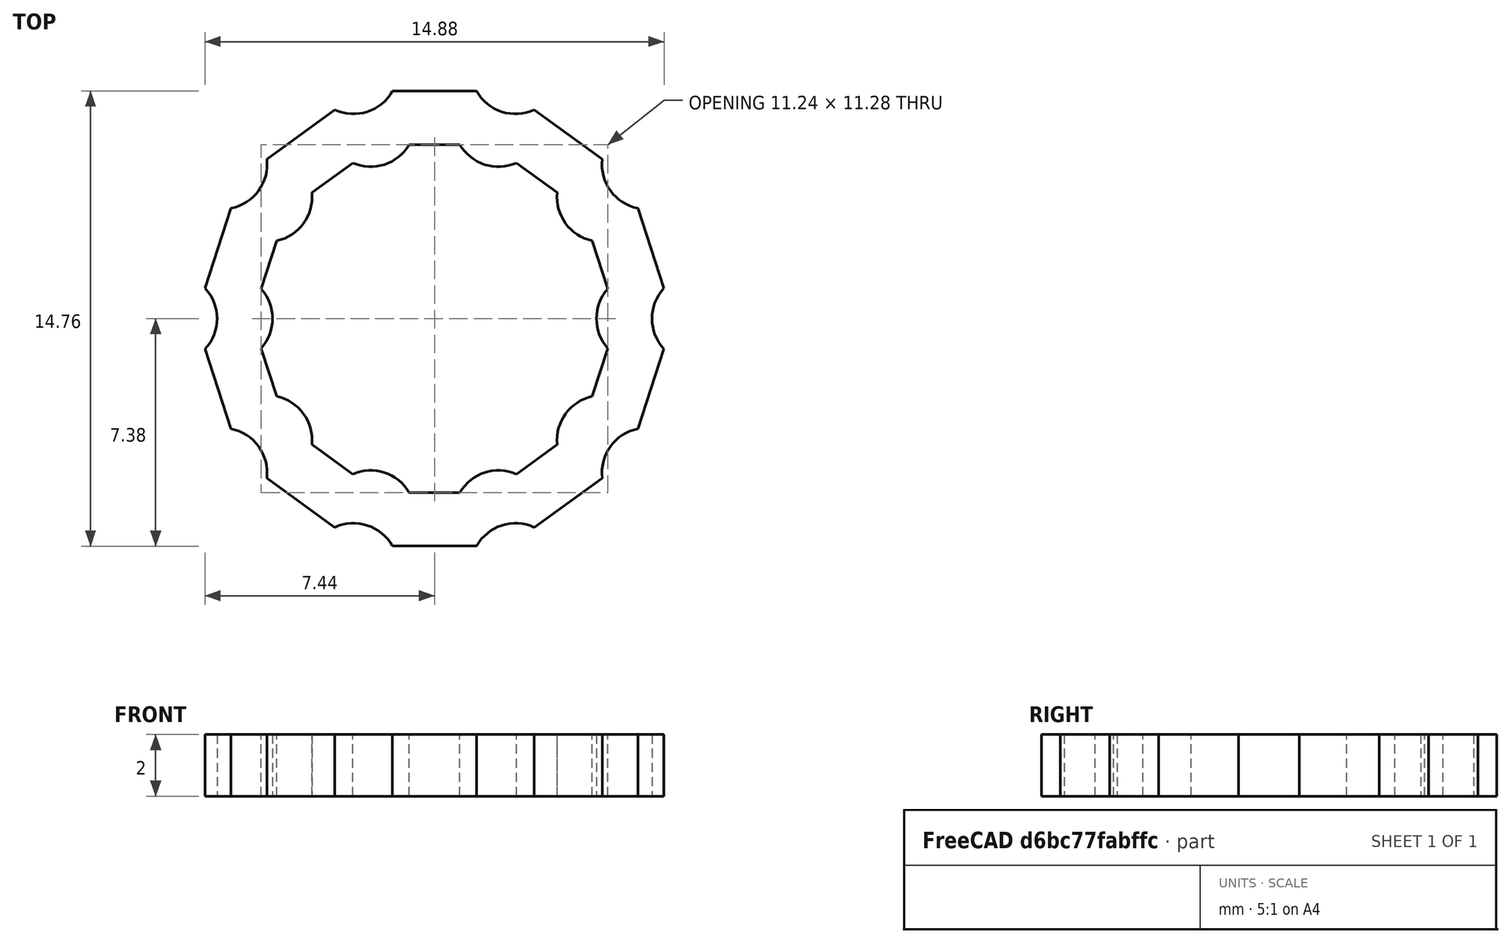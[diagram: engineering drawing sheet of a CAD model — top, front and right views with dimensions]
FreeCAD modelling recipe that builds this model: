
FCSTD DOCUMENT  (FreeCAD 0.19R)
Label: luer_lock_marker
License: All rights reserved
LicenseURL: http://en.wikipedia.org/wiki/All_rights_reserved
objects: Spreadsheet::Sheet×1, Sketcher::SketchObject×1, PartDesign::Pad×1, PartDesign::Body×1
note: 4 computed .brp shape members not serialized (recipe doc carries the construction recipe); baked Part::Feature solids carry a one-line shape summary decoded from their .brp

FEATURE [Spreadsheet::Sheet] Spreadsheet  label="var"
  cells = A1=thickness; B1(thickness)=1.8; A2=inner_radius; B2(inner_radius)=5.7000000000000002; A3=outer_radius; B3(outer_radius)==inner_radius + 1
FEATURE [Sketcher::SketchObject] CopySketch002  label="marker sketch"
  expr: Constraints[60] = <<var>>.outer_radius + <<var>>.thickness
  expr: Constraints[59] = <<var>>.inner_radius + <<var>>.thickness
  expr: Constraints[122] = <<var>>.outer_radius
  expr: Constraints[121] = <<var>>.inner_radius
  sketch-geometry (44):
    g0: Circle [constr] CenterX=0 CenterY=0 CenterZ=0 NormalX=0 NormalY=0 NormalZ=1 AngleXU=0 Radius=7.5
    g1: ArcOfCircle CenterX=2.62664 CenterY=8.08398 CenterZ=0 NormalX=0 NormalY=0 NormalZ=1 AngleXU=0 Radius=1.45 StartAngle=3.65219 EndAngle=5.14427
    g2: ArcOfCircle CenterX=6.87664 CenterY=4.99617 CenterZ=0 NormalX=0 NormalY=0 NormalZ=1 AngleXU=0 Radius=1.45 StartAngle=3.02387 EndAngle=4.51595
    g3: ArcOfCircle CenterX=6.87664 CenterY=-4.99617 CenterZ=0 NormalX=0 NormalY=0 NormalZ=1 AngleXU=0 Radius=1.45 StartAngle=1.76723 EndAngle=3.25932
    g4: ArcOfCircle CenterX=2.62664 CenterY=-8.08398 CenterZ=0 NormalX=0 NormalY=0 NormalZ=1 AngleXU=0 Radius=1.45 StartAngle=1.13891 EndAngle=2.631
    g5: ArcOfCircle CenterX=-2.62664 CenterY=-8.08398 CenterZ=0 NormalX=0 NormalY=0 NormalZ=1 AngleXU=0 Radius=1.45 StartAngle=0.510595 EndAngle=2.00268
    g6: ArcOfCircle CenterX=-6.87664 CenterY=-4.99617 CenterZ=0 NormalX=0 NormalY=0 NormalZ=1 AngleXU=0 Radius=1.45 StartAngle=6.16546 EndAngle=7.65755
    g7: ArcOfCircle CenterX=-8.5 CenterY=7e-16 CenterZ=0 NormalX=0 NormalY=0 NormalZ=1 AngleXU=0 Radius=1.45 StartAngle=5.53714 EndAngle=7.02923
    g8: ArcOfCircle CenterX=-6.87664 CenterY=4.99617 CenterZ=0 NormalX=0 NormalY=0 NormalZ=1 AngleXU=0 Radius=1.45 StartAngle=4.90883 EndAngle=6.40091
    g9: ArcOfCircle CenterX=-2.62664 CenterY=8.08398 CenterZ=0 NormalX=0 NormalY=0 NormalZ=1 AngleXU=0 Radius=1.45 StartAngle=4.28051 EndAngle=5.77259
    g10: ArcOfCircle CenterX=8.5 CenterY=0 CenterZ=0 NormalX=0 NormalY=0 NormalZ=1 AngleXU=0 Radius=1.45 StartAngle=2.39555 EndAngle=3.88763
    g11: Circle [constr] CenterX=0 CenterY=0 CenterZ=0 NormalX=0 NormalY=0 NormalZ=1 AngleXU=0 Radius=8.5
    g12: LineSegment StartX=-5.43668 StartY=5.16648 StartZ=0 EndX=-3.23359 EndY=6.76712 EndZ=0
    g13: LineSegment StartX=-1.36159 StartY=7.37537 StartZ=0 EndX=1.36159 EndY=7.37537 EndZ=0
    g14: LineSegment StartX=3.23359 StartY=6.76712 StartZ=0 EndX=5.43668 EndY=5.16648 EndZ=0
    g15: LineSegment StartX=6.59364 StartY=3.57406 StartZ=0 EndX=7.43515 EndY=0.984169 EndZ=0
    g16: LineSegment StartX=7.43515 StartY=-0.984169 StartZ=0 EndX=6.59364 EndY=-3.57406 EndZ=0
    g17: LineSegment StartX=3.23359 StartY=-6.76712 StartZ=0 EndX=5.43668 EndY=-5.16648 EndZ=0
    g18: LineSegment StartX=-1.36159 StartY=-7.37537 StartZ=0 EndX=1.36159 EndY=-7.37537 EndZ=0
    g19: LineSegment StartX=-5.43668 StartY=-5.16648 StartZ=0 EndX=-3.23359 EndY=-6.76712 EndZ=0
    g20: LineSegment StartX=-7.43515 StartY=-0.984169 StartZ=0 EndX=-6.59364 EndY=-3.57406 EndZ=0
    g21: LineSegment StartX=-6.59364 StartY=3.57406 StartZ=0 EndX=-7.43515 EndY=0.984169 EndZ=0
    g22: Circle [constr] CenterX=0 CenterY=0 CenterZ=0 NormalX=0 NormalY=0 NormalZ=1 AngleXU=0 Radius=6.7
    g23: Circle [constr] CenterX=0 CenterY=0 CenterZ=0 NormalX=0 NormalY=0 NormalZ=1 AngleXU=0 Radius=5.7
    g24: LineSegment StartX=5.61772 StartY=-0.964976 StartZ=0 EndX=5.11203 EndY=-2.52133 EndZ=0
    g25: LineSegment StartX=3.97764 StartY=-4.0827 StartZ=0 EndX=2.65372 EndY=-5.04458 EndZ=0
    g26: LineSegment StartX=0.818226 StartY=-5.64097 StartZ=0 EndX=-0.818226 EndY=-5.64097 EndZ=0
    g27: LineSegment StartX=-2.65372 StartY=-5.04458 StartZ=0 EndX=-3.97764 EndY=-4.0827 EndZ=0
    g28: LineSegment StartX=-5.11203 StartY=-2.52133 StartZ=0 EndX=-5.61772 EndY=-0.964976 EndZ=0
    g29: LineSegment StartX=-5.61772 StartY=0.964976 StartZ=0 EndX=-5.11203 EndY=2.52133 EndZ=0
    g30: LineSegment StartX=-3.97764 StartY=4.0827 StartZ=0 EndX=-2.65372 EndY=5.04458 EndZ=0
    g31: LineSegment StartX=-0.818226 StartY=5.64097 StartZ=0 EndX=0.818226 EndY=5.64097 EndZ=0
    g32: LineSegment StartX=2.65372 StartY=5.04458 StartZ=0 EndX=3.97764 EndY=4.0827 EndZ=0
    g33: LineSegment StartX=5.11203 StartY=2.52133 StartZ=0 EndX=5.61772 EndY=0.964976 EndZ=0
    g34: ArcOfCircle CenterX=5.42041 CenterY=-3.93816 CenterZ=0 NormalX=0 NormalY=0 NormalZ=1 AngleXU=0 Radius=1.45 StartAngle=1.78511 EndAngle=3.24144
    g35: ArcOfCircle CenterX=2.07041 CenterY=-6.37208 CenterZ=0 NormalX=0 NormalY=0 NormalZ=1 AngleXU=0 Radius=1.45 StartAngle=1.15679 EndAngle=2.61312
    g36: ArcOfCircle CenterX=-2.07041 CenterY=-6.37208 CenterZ=0 NormalX=0 NormalY=0 NormalZ=1 AngleXU=0 Radius=1.45 StartAngle=0.528473 EndAngle=1.9848
    g37: ArcOfCircle CenterX=-5.42041 CenterY=-3.93816 CenterZ=0 NormalX=0 NormalY=0 NormalZ=1 AngleXU=0 Radius=1.45 StartAngle=6.18334 EndAngle=7.63967
    g38: ArcOfCircle CenterX=-6.7 CenterY=-2.1e-15 CenterZ=0 NormalX=0 NormalY=0 NormalZ=1 AngleXU=0 Radius=1.45 StartAngle=5.55502 EndAngle=7.01135
    g39: ArcOfCircle CenterX=-5.42041 CenterY=3.93816 CenterZ=0 NormalX=0 NormalY=0 NormalZ=1 AngleXU=0 Radius=1.45 StartAngle=4.9267 EndAngle=6.38303
    g40: ArcOfCircle CenterX=-2.07041 CenterY=6.37208 CenterZ=0 NormalX=0 NormalY=0 NormalZ=1 AngleXU=0 Radius=1.45 StartAngle=4.29838 EndAngle=5.75471
    g41: ArcOfCircle CenterX=2.07041 CenterY=6.37208 CenterZ=0 NormalX=0 NormalY=0 NormalZ=1 AngleXU=0 Radius=1.45 StartAngle=3.67007 EndAngle=5.12639
    g42: ArcOfCircle CenterX=5.42041 CenterY=3.93816 CenterZ=0 NormalX=0 NormalY=0 NormalZ=1 AngleXU=0 Radius=1.45 StartAngle=3.04175 EndAngle=4.49808
    g43: ArcOfCircle CenterX=6.7 CenterY=0 CenterZ=0 NormalX=0 NormalY=0 NormalZ=1 AngleXU=0 Radius=1.45 StartAngle=2.41343 EndAngle=3.86976
  constraints (142):
    c: PointOnObject(g1,g0)
    c: PointOnObject(g1,g0)
    c: PointOnObject(g2,g0)
    c: PointOnObject(g2,g0)
    c: PointOnObject(g3,g0)
    c: PointOnObject(g3,g0)
    c: PointOnObject(g4,g0)
    c: PointOnObject(g4,g0)
    c: PointOnObject(g5,g0)
    c: PointOnObject(g5,g0)
    c: PointOnObject(g6,g0)
    c: PointOnObject(g6,g0)
    c: PointOnObject(g7,g0)
    c: PointOnObject(g7,g0)
    c: PointOnObject(g8,g0)
    c: PointOnObject(g9,g0)
    c: PointOnObject(g9,g0)
    c: PointOnObject(g10,g0)
    c: PointOnObject(g10,g0)
    c: Equal(g1,g2)
    c: Equal(g1,g10)
    c: Equal(g1, g3-g9) x7
    c: PointOnObject(g1,g11)
    c: PointOnObject(g2,g11)
    c: PointOnObject(g10,g11)
    c: PointOnObject(g3,g11)
    c: PointOnObject(g4,g11)
    c: PointOnObject(g5,g11)
    c: PointOnObject(g6,g11)
    c: PointOnObject(g7,g11)
    c: PointOnObject(g8,g11)
    c: PointOnObject(g9,g11)
    c: Coincident(g12,g8)
    c: Coincident(g12,g9)
    c: Coincident(g13,g9)
    c: Coincident(g13,g1)
    c: Coincident(g14,g1)
    c: Coincident(g14,g2)
    c: PointOnObject(g8,g0)
    c: Coincident(g15,g2)
    c: Coincident(g16,g10)
    c: Coincident(g17,g4)
    c: Coincident(g17,g3)
    c: Coincident(g18,g5)
    c: Coincident(g18,g4)
    c: Coincident(g19,g6)
    c: Coincident(g19,g5)
    c: Coincident(g20,g7)
    c: Coincident(g20,g6)
    c: Coincident(g21,g8)
    c: Coincident(g15,g10)
    c: Coincident(g16,g3)
    c: Coincident(g21,g7)
    c: Radius(g0) = 7.5
    c: Radius(g11) = 8.5
    c: Equal(g16,g15)
    c: Equal(g15,g14)
    c: Equal(g14,g13)
    c: Equal(g13,g12)
    c: Equal(g12,g21)
    c: Equal(g21,g20)
    c: Equal(g20,g19)
    c: Equal(g19,g18)
    c: Equal(g18,g17)
    c: Radius(g2) = 1.45
    c: Coincident(g0,g11)
    c: PointOnObject(g24,g23)
    c: PointOnObject(g24,g23)
    c: PointOnObject(g25,g23)
    c: PointOnObject(g25,g23)
    c: PointOnObject(g26,g23)
    c: PointOnObject(g26,g23)
    c: PointOnObject(g27,g23)
    c: PointOnObject(g27,g23)
    c: PointOnObject(g28,g23)
    c: PointOnObject(g28,g23)
    c: PointOnObject(g29,g23)
    c: PointOnObject(g29,g23)
    c: PointOnObject(g30,g23)
    c: PointOnObject(g30,g23)
    c: PointOnObject(g31,g23)
    c: PointOnObject(g31,g23)
    c: PointOnObject(g32,g23)
    c: PointOnObject(g32,g23)
    c: PointOnObject(g33,g23)
    c: PointOnObject(g33,g23)
    c: PointOnObject(g34,g22)
    c: Coincident(g34,g25)
    c: Coincident(g34,g24)
    c: PointOnObject(g35,g22)
    c: Coincident(g35,g25)
    c: Coincident(g35,g26)
    c: PointOnObject(g36,g22)
    c: Coincident(g36,g26)
    c: Coincident(g36,g27)
    c: PointOnObject(g37,g22)
    c: Coincident(g37,g27)
    c: Coincident(g37,g28)
    c: PointOnObject(g38,g22)
    c: Coincident(g38,g28)
    c: Coincident(g38,g29)
    c: PointOnObject(g39,g22)
    c: Coincident(g39,g29)
    c: Coincident(g39,g30)
    c: PointOnObject(g40,g22)
    c: Coincident(g40,g30)
    c: Coincident(g40,g31)
    c: Coincident(g41,g31)
    c: Coincident(g41,g32)
    c: PointOnObject(g42,g22)
    c: Coincident(g42,g32)
    c: Coincident(g42,g33)
    c: PointOnObject(g43,g22)
    c: Coincident(g43,g33)
    c: Coincident(g43,g24)
    c: Radius(g23) = 5.7
    c: Radius(g22) = 6.7
    c: PointOnObject(g41,g22)
    c: Equal(g24,g25)
    c: Equal(g25,g26)
    c: Equal(g26,g27)
    c: Equal(g27,g28)
    c: Equal(g28,g29)
    c: Equal(g29,g30)
    c: Equal(g30,g31)
    c: Equal(g31,g32)
    c: Equal(g32,g33)
    c: Equal(g34,g43)
    c: Equal(g43,g42)
    c: Equal(g42,g41)
    c: Equal(g41,g40)
    c: Equal(g40,g39)
    c: Equal(g39,g38)
    c: Equal(g38,g37)
    c: Equal(g37,g36)
    c: Equal(g36,g35)
    c: Radius(g43) = 1.45
    c: Coincident(g0,g-1)
    c: Coincident(g23,g22)
    c: PointOnObject(g10,g-1)
    c: PointOnObject(g43,g-1)
    c: Coincident(g22,g-1)
FEATURE [PartDesign::Pad] Pad001  label="marker"
  Length = 2
  Length2 = 100
  Profile = -> CopySketch002
  Type = 0
FEATURE [PartDesign::Body] Body001  label="marker body"
  Group = -> [Pad001]
  Origin = -> Origin001
  Tip = -> Pad001
